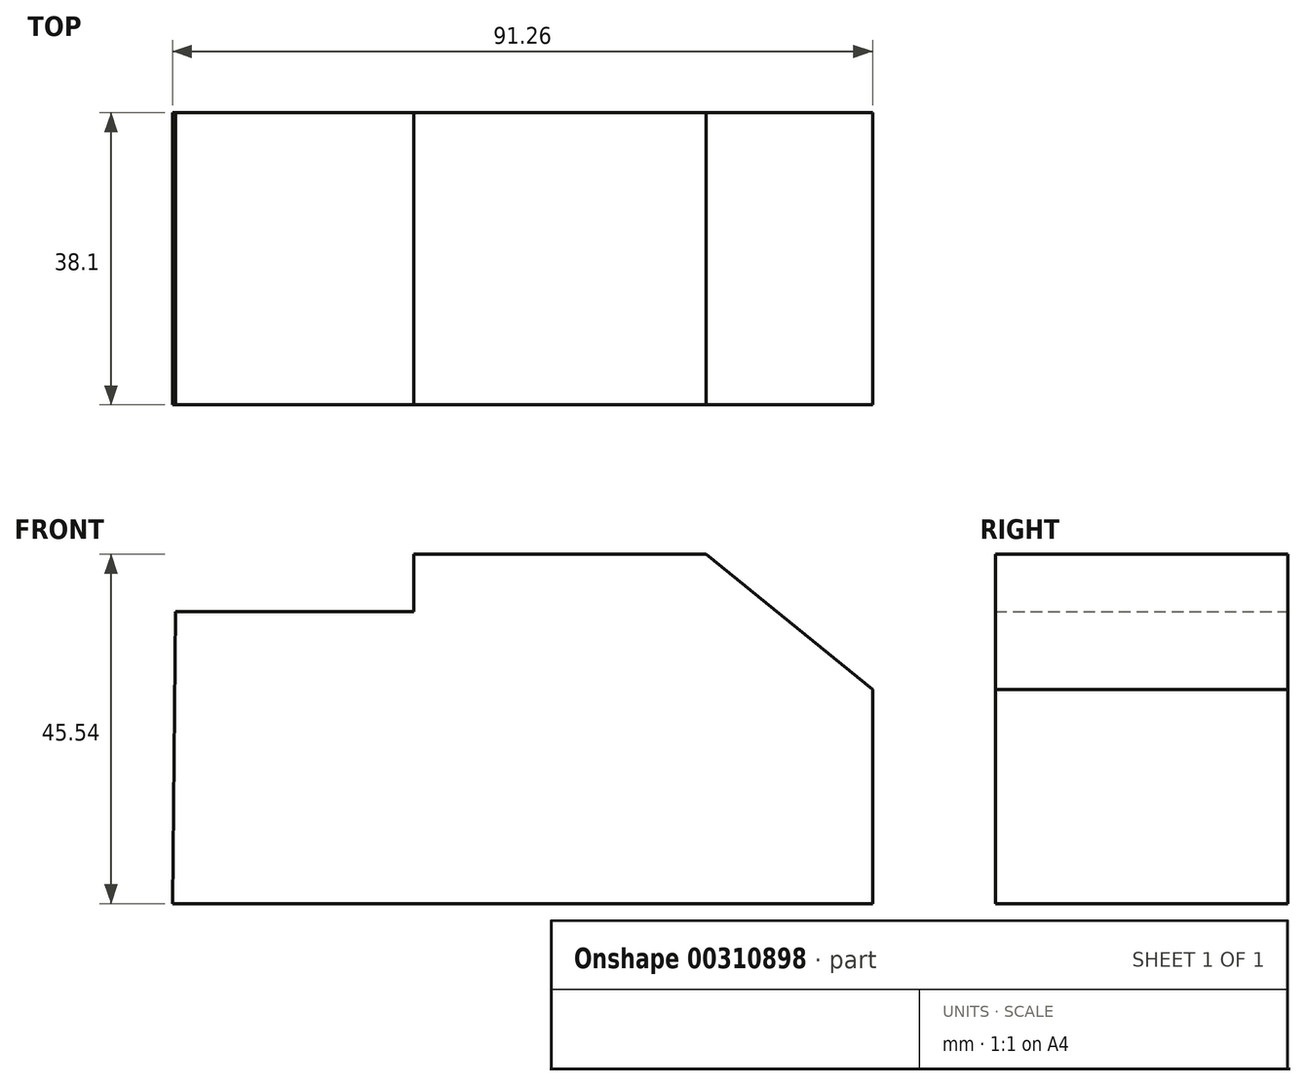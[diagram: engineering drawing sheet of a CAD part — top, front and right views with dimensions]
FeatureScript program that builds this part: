
annotation { "Feature Type Name" : "Feature", "Feature Type Description" : "" }
export const myFeature = defineFeature(function(context is Context, id is Id, definition is map)
    precondition{}
    {
        {
            var Q0;
            Q0=qCreatedBy(makeId("Front.planeOp"),FACE);
            var sketch = newSketch(context, id + "F0", { "sketchPlane" : qUnion([Q0])});
            skLineSegment(sketch, "E0", {"start": v(-71.45, -45.54) * mm, "end": v(19.8, -45.54) * mm});
            skLineSegment(sketch, "E1", {"start": v(19.8, -45.54) * mm, "end": v(19.8, -17.6) * mm});
            skLineSegment(sketch, "E2", {"start": v(19.8, -17.6) * mm, "end": v(-1.9, 0) * mm});
            skLineSegment(sketch, "E3", {"start": v(-1.9, 0) * mm, "end": v(-40, 0) * mm});
            skLineSegment(sketch, "E4", {"start": v(-40, 2.72) * mm, "end": v(-40, -7.44) * mm});
            skLineSegment(sketch, "E5", {"start": v(-40, -7.44) * mm, "end": v(-71.05, -7.44) * mm});
            skLineSegment(sketch, "E6", {"start": v(-71.05, -7.44) * mm, "end": v(-71.45, -45.54) * mm});
            skSolve(sketch);
        }
        {
            var Q0;
            Q0=makeQuery(id+"F0.imprint","IMPRINT",FACE,{"disambiguationData":[TD([[makeQuery(id+"F0.imprint","IMPRINT",EDGE,{"derivedFrom":sQuery(id+"F0.wireOp",EDGE,"E0")}),1.0]])]});
            extrude(context, id + "F1", {"entities" : qUnion([Q0]), "depth" : 38.1 * mm});
        }
    });
